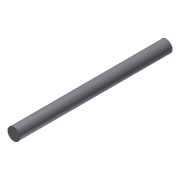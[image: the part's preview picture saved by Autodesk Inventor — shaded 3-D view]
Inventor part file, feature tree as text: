
AUTODESK INVENTOR PART (.ipt)
format: ipt  version: 2012 (Build 160160000, 160)  size: 67,072 bytes
history: native  units: in
note: dims shown in document units (in); Inventor stores cm internally (conversion verified against a paired STEP export)
features: extrude x1, sketch x1
ambient origin geometry x8: Origin, YZ Plane, XZ Plane, XY Plane, X Axis, Y Axis, Z Axis, Center Point
bodies: Solid1 (feature_tree)
feature tree (2):
  extrude  "Extrusion1"  Depth=6.25in TaperAngle=0.0deg
  sketch  "Sketch1"  dims[d0=0.5in d1=6.25in d2=0.0in]
